# Revit family: Verano_V282_Oviedo_GM_R21
name_source: partatom
category: Generic Models
units: mm (PartAtom-declared; Revit-internal decimal feet)

## family parameters
Always vertical = Yes
Can host rebar = No
Cut with Voids When Loaded = No
Part Type = Normal
Room Calculation Point = No
Round Connector Dimension = Use Diameter
Shared = No
Work Plane-Based = No

## types (4) — shared parameters
L7 = 3450 mm  [stored 11.3189 ft]
L8 = 2250 mm
Manufacturer = Verano Systems
Model = V282 Oviedo
URL = https://verano.nl
zero-valued in all types: Default Elevation

## per-type parameters (varying)
| type | 1 - Ausfall 2000 | 2 - Ausfall 2500 | 3 - Ausfall 3000 | 4 - Ausfall 3500 | TYPE (1 - 4) |
| 2000 Projection | Yes | No | No | No | 1 |
| 2500 Projection | No | Yes | No | No | 2 |
| 3000 Projection | No | No | Yes | No | 3 |
| 3500 Projection | No | No | No | Yes | 4 |

note: [stored X ft] marks values corroborated as IEEE doubles in the binary element streams (Revit-internal decimal feet)

## geometry (parser evidence)
native form markers: Extrusion x1, Sweep x62
no freeform markers — native parametric forms only
